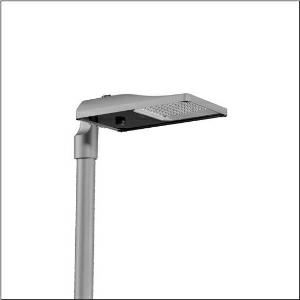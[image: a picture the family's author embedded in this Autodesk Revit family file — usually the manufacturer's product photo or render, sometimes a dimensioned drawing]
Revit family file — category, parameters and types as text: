
# Revit family: streetlight_sl_31_midi___st1_0a_5xh3d71t08qa_5396
name_source: partatom
category: Lighting Fixtures
units: mm (PartAtom-declared; Revit-internal decimal feet)

## family parameters
Cut with Voids When Loaded = No
Host = Face
Light Source = No
Part Type = Normal
Room Calculation Point = No
Round Connector Dimension = Use Diameter
Shared = No

## types (1)
- --- (1 x LED, 19710 lm, 163.8 W, 2200K)
    Apparent Load = 164 VA
    CIE Flux Codes = 40 73 97 100 100
    Color Rendering = 70
    Color Temperature = 2200K
    Default Elevation = 1800 mm
    Description = Streetlight SL 31 midi D4i, Desk-Remote mast luminaire for post-top, side-entry; light control with lens of PMMA; light distribution: ST1.0a, direct asymmetric distribution, for standard-compliant lighting for roads and squares; LED: luminous flux: 19.710lm, light colour: 722, colour temperature: 2200K; luminous efficacy: 120,3lm/W; control: pre-setting: logarithmic dimming characteristic, flexible luminous flux parameterisation, time-dependent luminous flux control, constant luminous flux control, power reduction, intelligent temperature release in ECG and LED module, overheat protection; luminaire housing, of diecast aluminium, SITECO metallic grey (DB 702S), corrosivity category C5 high according to DIN EN ISO 12944; cover of toughened safety glass, transparent, mast flange of diecast aluminium, SITECO metallic grey (DB 702S), spigot size: 76/60mm, mast flange included unmounted; with cable H07RN-F 2x 1.5mm², cable length: 14,5m, connection cable pre-assembled; mains connection: 220..240V, AC, 50/60Hz; power consumption (at start of service life): 163,8W / (at end of service life): 179W / (with reduced operation 50%): 72,6W; protection rating (complete): IP66; insulation class (complete): insulation class II (safety insulation); impact resistance: IK09; certification: CE, ENEC, ENEC+, VDE, UKCA, ZD4i; permissible operating ambient temperature for outdoor applications: -40..+50°C; packaging unit: 1 piece

Light Distribution: ST1.0a
    Height = 79 mm
    Lamp = 1 x LED
    Lamp Light Flux = 19710 lm
    Lamp Power = 163.8 W
    Lamp count = 1
    Length = 577 mm
    Luminous efficacy = 120 lm/W
    Manufacturer = Siteco
    ModVariant = No
    Model = 5XH3D71T08QA
    Number of Poles = 1
    OnlyDefault = Yes
    Power Factor = 1
    Product Name = Streetlight SL 31 midi | ST1.0a
    Product group = mast luminaire | pylon top
    ProductGroupID = 6100
    Protection Class = Protection class II
    Protection Degree = IP 66
    RLX_Detail_Level = 1
    RLX_Emergency_Light_Flux = 0 lm
    RLX_Emergency_Type = 0
    RLX_Emergency_Type_DB = No
    RlxData = <blob elided: 26513 chars, md5=b6119251>
    Socket = socket
    Standby Power = 0 W
    System Light Flux = 19710 lm
    System Power = 164 W
    Type Comments = factory setting: luminous flux: 100 % | dim-lin: 254 | 865 mA
    Type Image = l_1300321.jpg
    URL = http://relux.com
    VarID = @adj_009163
    Voltage = 0 V
    Weight = 0.00 kg
    Width = 362 mm

## geometry (parser evidence)
native form markers: Blend x4, Sweep x11
no freeform markers — native parametric forms only
